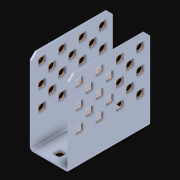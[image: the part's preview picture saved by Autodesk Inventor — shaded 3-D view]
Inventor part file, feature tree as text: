
AUTODESK INVENTOR PART (.ipt)
format: ipt  version: 2021 (Build 250183000, 183)  size: 630,272 bytes
history: native  units: in
note: dims shown in document units (in); Inventor stores cm internally (conversion verified against a paired STEP export)
features: other x41, extrude x40, pattern_linear x5, sketch x2, imported_body x1
ambient origin geometry x8: Origin, YZ Plane, XZ Plane, XY Plane, X Axis, Y Axis, Z Axis, Center Point
bodies: Body1 (feature_tree), Body2 (feature_tree), Body3 (feature_tree), Body4 (feature_tree), Body5 (feature_tree), Body6 (feature_tree), Body7 (feature_tree), Body8 (feature_tree), Body9 (feature_tree), Body10 (feature_tree), Body11 (feature_tree), Body12 (feature_tree), Body13 (feature_tree), Body14 (feature_tree), Body15 (feature_tree), Body16 (feature_tree), Body17 (feature_tree), Body18 (feature_tree), Body19 (feature_tree), Body20 (feature_tree), Body21 (feature_tree), Body22 (feature_tree), Body23 (feature_tree), Body24 (feature_tree), Body25 (feature_tree), Body26 (feature_tree), Body27 (feature_tree), Body28 (feature_tree), Body29 (feature_tree), Body30 (feature_tree), Body31 (feature_tree), Body32 (feature_tree), Body33 (feature_tree), Body34 (feature_tree), Body35 (feature_tree), Body36 (feature_tree), Body37 (feature_tree), Body38 (feature_tree), Body39 (feature_tree), Body40 (feature_tree), Body41 (feature_tree)
feature tree (89):
  parser-record x1  (decoder bookkeeping rows leaked as tree rows — omitted from the tree; the rows remain in map.json)
  imported_body  "Base1"
  pattern_linear  "Rectangular Pattern1"  Count1=4 Spacing1=0.5in
  pattern_linear  "Rectangular Pattern2"  Count1=3 Spacing1=0.5in
  pattern_linear  "Rectangular Pattern3"  Spacing1=0.046in  [1 undecoded]
  pattern_linear  "Rectangular Pattern4"  Count1=3 Spacing1=0.5in
  pattern_linear  "Rectangular Pattern5"  Count1=2 Spacing1=0.5in
  other  "Srf1"
  other  "Srf2"
  other  "Srf3"
  other  "Srf4"
  other  "Srf5"
  other  "Srf6"
  other  "Srf7"
  other  "Srf8"
  other  "Srf9"
  other  "Srf10"
  other  "Srf11"
  other  "Srf12"
  sketch  "Sketch2"  dims[d40=0.046in d41=0.0in d42=1.5748in d44=0.5in d45=1.1811in d47=0.5in]
  other  "Srf13"
  other  "Srf14"
  other  "Srf15"
  other  "Srf16"
  other  "Srf17"
  other  "Srf18"
  other  "Srf19"
  other  "Srf20"
  other  "Srf21"
  other  "Srf22"
  other  "Srf23"
  other  "Srf24"
  other  "Srf25"
  other  "Srf26"
  other  "Srf27"
  other  "Srf28"
  other  "Srf29"
  other  "Srf30"
  sketch  "Sketch4"  dims[d48=0.167in d49=0.046in d50=0.0in d51=1.1811in d53=0.5in d54=0.7874in d56=0.5in d58=0.046in d59=0.0in d60=1.5748in d62=0.5in d63=1.1811in d65=0.5in d67=0.046in d68=0.0in d69=1.1811in d71=0.5in d72=0.7874in d74=0.5in d76=0.046in d77=0.0in d78=1.5748in d80=0.5in]
  other  "Srf31"
  other  "Srf32"
  other  "Srf33"
  other  "Srf34"
  other  "Srf35"
  other  "Srf36"
  other  "Srf37"
  other  "Srf38"
  other  "Srf39"
  other  "Srf40"
  extrude  "ExtrusionSrf1"  Depth=0.046in TaperAngle=0.0deg
  extrude  "ExtrusionSrf13"  Depth=0.5in
  extrude  "ExtrusionSrf19"  Depth=0.5in
  extrude  "ExtrusionSrf31"  Depth=0.046in TaperAngle=0.0deg
  extrude  "ExtrusionSrf37"  Depth=0.5in
  extrude  "ExtrusionSrf2"  Depth=0.5in
  extrude  "ExtrusionSrf3"  Depth=0.046in TaperAngle=0.0deg
  extrude  "ExtrusionSrf4"  Depth=0.5in
  extrude  "ExtrusionSrf5"  [1 undecoded]
  extrude  "ExtrusionSrf6"  [1 undecoded]
  extrude  "ExtrusionSrf7"  [1 undecoded]
  extrude  "ExtrusionSrf8"  [1 undecoded]
  extrude  "ExtrusionSrf9"  [1 undecoded]
  extrude  "ExtrusionSrf10"  [1 undecoded]
  extrude  "ExtrusionSrf11"  [1 undecoded]
  extrude  "ExtrusionSrf12"  [1 undecoded]
  extrude  "ExtrusionSrf14"  [1 undecoded]
  extrude  "ExtrusionSrf15"  [1 undecoded]
  extrude  "ExtrusionSrf16"  [1 undecoded]
  extrude  "ExtrusionSrf17"  [1 undecoded]
  extrude  "ExtrusionSrf18"  [1 undecoded]
  extrude  "ExtrusionSrf20"  [1 undecoded]
  extrude  "ExtrusionSrf21"  [1 undecoded]
  extrude  "ExtrusionSrf22"  [1 undecoded]
  extrude  "ExtrusionSrf23"  [1 undecoded]
  extrude  "ExtrusionSrf24"  [1 undecoded]
  extrude  "ExtrusionSrf25"  [1 undecoded]
  extrude  "ExtrusionSrf26"  [1 undecoded]
  extrude  "ExtrusionSrf27"  [1 undecoded]
  extrude  "ExtrusionSrf28"  [1 undecoded]
  extrude  "ExtrusionSrf29"  [1 undecoded]
  extrude  "ExtrusionSrf30"  [1 undecoded]
  extrude  "ExtrusionSrf32"  [1 undecoded]
  extrude  "ExtrusionSrf33"  [1 undecoded]
  extrude  "ExtrusionSrf34"  [1 undecoded]
  extrude  "ExtrusionSrf35"  [1 undecoded]
  extrude  "ExtrusionSrf36"  [1 undecoded]
  extrude  "ExtrusionSrf38"  [1 undecoded]
  extrude  "ExtrusionSrf39"  [1 undecoded]
  extrude  "ExtrusionSrf40"  [1 undecoded]
note: 33 required parameter values undecoded (feature->parameter linkage not recoverable at this tier; creation-order binding heuristic only, values carry confidence <= 0.55)
